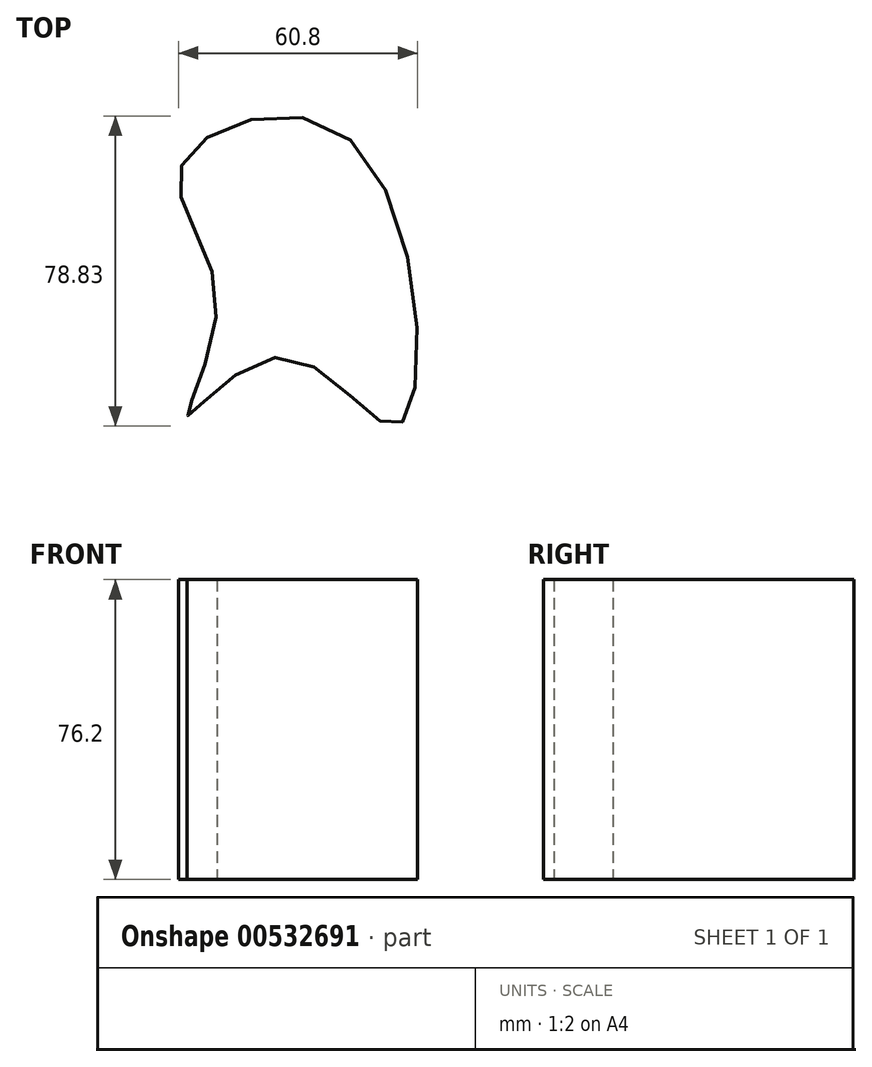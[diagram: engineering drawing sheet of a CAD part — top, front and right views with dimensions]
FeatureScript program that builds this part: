
annotation { "Feature Type Name" : "Feature", "Feature Type Description" : "" }
export const myFeature = defineFeature(function(context is Context, id is Id, definition is map)
    precondition{}
    {
        {
            var Q0;
            Q0=qCreatedBy(makeId("Top.planeOp"),FACE);
            var sketch = newSketch(context, id + "F0", { "sketchPlane" : qUnion([Q0])});
            skFitSpline(sketch, "E0", {"points": [v(13.16, 36.4) * mm, v(-29.8, 29.77) * mm, v(-20.77, -3.97) * mm, v(-28.14, -33.65) * mm, v(-3.44, -18.71) * mm, v(25.32, -36.04) * mm, v(13.16, 36.4) * mm]});
            skSolve(sketch);
        }
        {
            var Q0;
            Q0 = qSketchRegion(id + "F0", true);
            extrude(context, id + "F1", {"entities" : qUnion([Q0]), "depth" : 76.2 * mm, "offsetDistance" : 25.4 * mm});
        }
    });
